# Revit family: PGR_Noken_ShwrFitngsPckge_SMART
name_source: partatom
category: Plumbing Fixtures
revit_build: Autodesk Revit 2017 (Build: 20190508_0315(x64)
units: mm (PartAtom-declared; Revit-internal decimal feet)

## family parameters
Always vertical = Yes
Cut with Voids When Loaded = No
Host = Wall
OmniClass Number = 23.45.05.14.17
OmniClass Title = Showers
Part Type = Normal
Room Calculation Point = No
Round Connector Dimension = Use Diameter
Shared = No

## types (1)
- Thermostatic-100093268
    AccessibilityPerformance = See ProductInformation for technical PDF
    AssetType = Fixed
    BIMObjectName = PGR_Noken_ShowerFittingsPackage_SMART_Chrome-100093268
    CWFU = 0
    Category = Pr_40_20_87_75: Shower fittings package
    CodePerformance = EN 1112, EN 248, EN 1111
    Collection = SMART
    Color = Chrome
    Constituents = Componentes que forman el pack
    DiameterCW = 20 mm
    DiameterHW = 20 mm
    DrainSize = 0 mm
    DurationUnit = year
    Features = See ProductInformation for technical PDF
    Finish = chrome
    FlowPressure = 0.0
    HWFU = 0
    HasTray = No
    Height = 900 mm  [stored 2.95276 ft]
    IfcExportAs = IfcSanitaryTerminalType
    IfcExportType = Shower
    ManufacturerURL = www.noken.com
    Material = Brass
    MaterialMetal = PGR_Noken_Brass_Chrome
    MaterialThickness = 0 mm  [stored 0 ft]
    Model = 100093268
    ModelNumber = 100093268
    ModelReference = Smart shower package
    NBSDescription = Shower fittings package
    NBSReference = 45-35-70/330
    Name = ShowerFittingsPackage_SMART_Chrome-100093268
    NettWeight = 0
    NominalDepth = 1150 mm
    NominalHeight = 1150 mm
    NominalLength = 541 mm  [stored 1.77493 ft]
    NominalWidth = 288 mm  [stored 0.944882 ft]
    ProductInformation = https://pdfgenerator.porcelanosagrupo.com
    Reference = -
    Shape = Round
    ShowerType = UNSET
    Size = 541x288x1150mm
    Status = UNSET
    SustainabilityPerformance = See ProductInformation for technical PDF
    Type Image = 100093268.jpg
    URL = www.noken.com
    Uniclass2015Code = Pr_40_20_87_75
    Uniclass2015Title = Shower fittings package
    Uniclass2015Version = V1_14
    ValveType = Thermostatic Mixer
    Version = 1
    WarrantyDescription = See ProductInformation for technical PDF
    WarrantyDurationUnit = year

note: source unit labels omitted for FlowPressure — the stored unit's dimension contradicts the parameter name (converter mislabeling)

note: [stored X ft] marks values corroborated as IEEE doubles in the binary element streams (Revit-internal decimal feet)

## geometry (parser evidence)
native form markers: Blend x4, Sweep x6
no freeform markers — native parametric forms only
